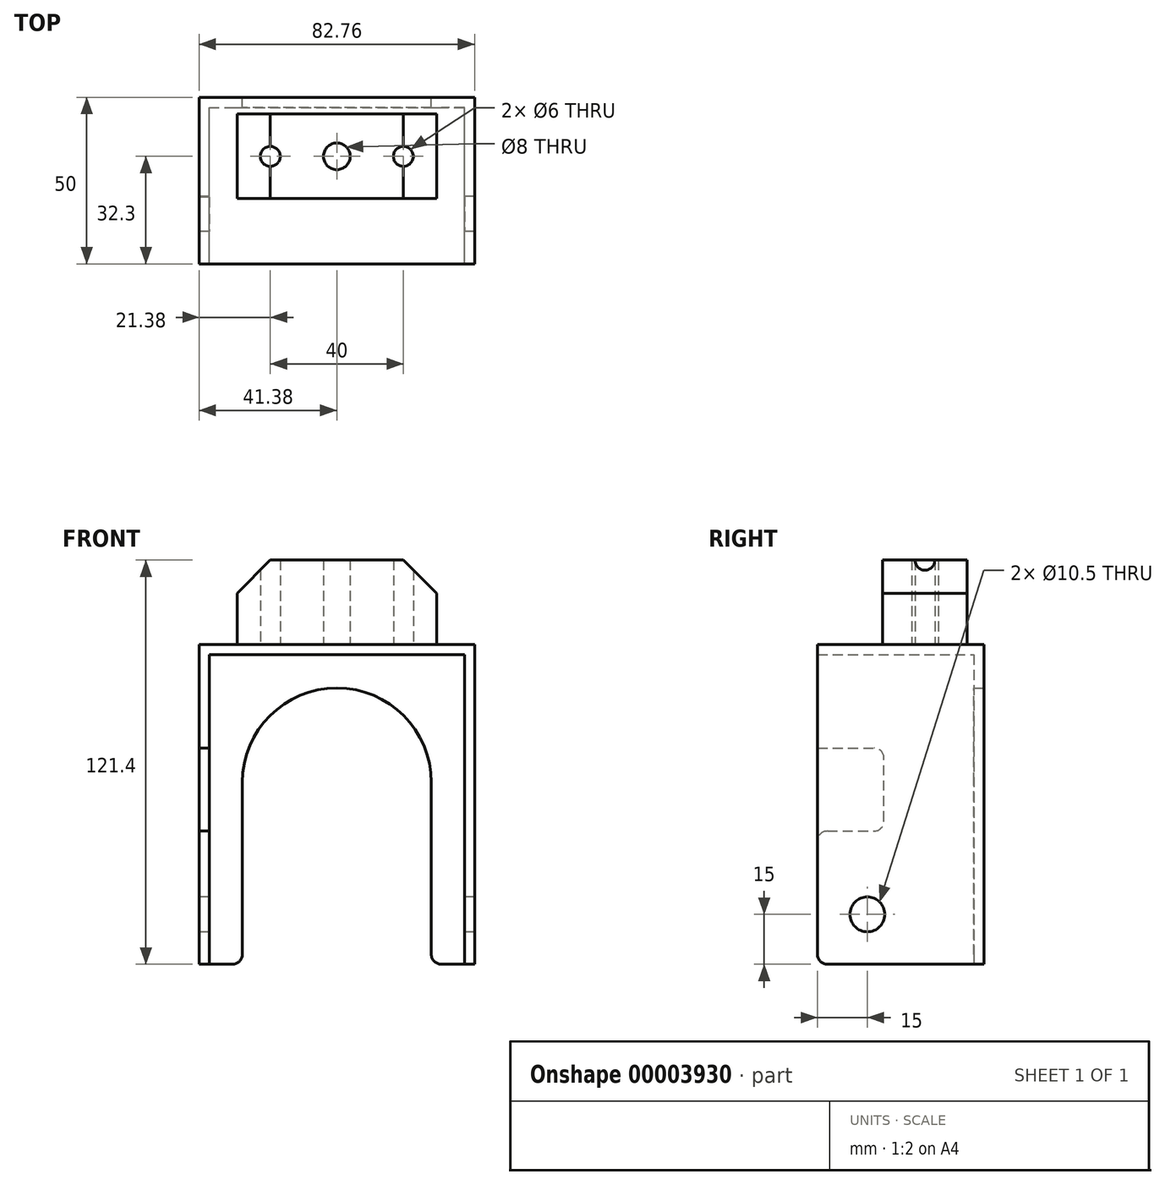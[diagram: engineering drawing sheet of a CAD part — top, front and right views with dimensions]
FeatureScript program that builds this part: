
annotation { "Feature Type Name" : "Feature", "Feature Type Description" : "" }
export const myFeature = defineFeature(function(context is Context, id is Id, definition is map)
    precondition{}
    {
        {
            var Q0;
            Q0=qCreatedBy(makeId("Front.planeOp"),FACE);
            var sketch = newSketch(context, id + "F0", { "sketchPlane" : qUnion([Q0])});
            skLineSegment(sketch, "E0", {"start": v(-38.38, 0) * mm, "end": v(0, 0) * mm});
            skLineSegment(sketch, "E1", {"start": v(0, 0) * mm, "end": v(38.38, 0) * mm});
            skLineSegment(sketch, "E2", {"start": v(-38.38, 0) * mm, "end": v(-38.38, -93) * mm});
            skLineSegment(sketch, "E3", {"start": v(38.38, 0) * mm, "end": v(38.38, -93) * mm});
            skLineSegment(sketch, "E4", {"start": v(-38.38, -93) * mm, "end": v(-28.37, -93) * mm});
            skLineSegment(sketch, "E5", {"start": v(-28.38, -93) * mm, "end": v(-28.38, -38.38) * mm});
            skLineSegment(sketch, "E6", {"start": v(38.38, -93) * mm, "end": v(28.37, -93) * mm});
            skLineSegment(sketch, "E7", {"start": v(28.37, -93) * mm, "end": v(28.37, -38.38) * mm});
            skArc(sketch, "E8", {"start": v(28.38, -38.38) * mm, "mid": v(0, -10) * mm, "end": v(-28.37, -38.38) * mm});
            skLineSegment(sketch, "E9.0", {"start": v(-41.38, 3) * mm, "end": v(-41.38, -93) * mm});
            skLineSegment(sketch, "E9.1", {"start": v(-41.38, 3) * mm, "end": v(0, 3) * mm});
            skLineSegment(sketch, "E9.2", {"start": v(0, 3) * mm, "end": v(41.38, 3) * mm});
            skLineSegment(sketch, "E9.3", {"start": v(41.38, 3) * mm, "end": v(41.38, -93) * mm});
            skLineSegment(sketch, "E10", {"start": v(-41.38, -93) * mm, "end": v(-38.38, -93) * mm});
            skLineSegment(sketch, "E11", {"start": v(38.38, -93) * mm, "end": v(41.38, -93) * mm});
            skLineSegment(sketch, "E12", {"start": v(-16.37, -93) * mm, "end": v(-16.38, -22) * mm, "construction": true});
            skLineSegment(sketch, "E13", {"start": v(-16.38, -22) * mm, "end": v(16.37, -22) * mm, "construction": true});
            skLineSegment(sketch, "E14", {"start": v(16.37, -22) * mm, "end": v(16.38, -93) * mm, "construction": true});
            skLineSegment(sketch, "E15", {"start": v(-41.38, 3) * mm, "end": v(-16.38, -22) * mm, "construction": true});
            skLineSegment(sketch, "E16", {"start": v(16.37, -22) * mm, "end": v(41.38, 3) * mm, "construction": true});
            skSolve(sketch);
        }
        {
            var Q0;
            Q0=makeQuery(id+"F0.imprint","IMPRINT",FACE,{"disambiguationData":[TD([[makeQuery(id+"F0.imprint","IMPRINT",EDGE,{"derivedFrom":sQuery(id+"F0.wireOp",EDGE,"E0")}),-1.0]])]});
            extrude(context, id + "F1", {"entities" : qUnion([Q0]), "depth" : 3 * mm});
        }
        {
            var Q0;
            Q0=makeQuery(id+"F0.imprint","IMPRINT",FACE,{"disambiguationData":[TD([[makeQuery(id+"F0.imprint","IMPRINT",EDGE,{"derivedFrom":sQuery(id+"F0.wireOp",EDGE,"E0")}),1.0]])]});
            extrude(context, id + "F2", {"entities" : qUnion([Q0]), "operationType" : NewBodyOperationType.ADD, "depth" : 50 * mm});
        }
        {
            var Q0;
            Q0=makeQuery(id+"F2.opExtrude","SWEPT_FACE",FACE,{"disambiguationData":[OSD([sQuery(id+"F0.wireOp",EDGE,"E9.0")])]});
            var sketch = newSketch(context, id + "F3", { "sketchPlane" : qUnion([Q0])});
            skCircle(sketch, "E17", {"center": v(35, -78) * mm, "radius": 5.25 * mm});
            skLineSegment(sketch, "E18.bottom", {"start": v(50, -53) * mm, "end": v(30, -53) * mm});
            skLineSegment(sketch, "E18.top", {"start": v(50, -28) * mm, "end": v(30, -28) * mm});
            skLineSegment(sketch, "E18.left", {"start": v(50, -53) * mm, "end": v(50, -28) * mm});
            skLineSegment(sketch, "E18.right", {"start": v(30, -53) * mm, "end": v(30, -28) * mm});
            skSolve(sketch);
        }
        {
            var Q0;
            Q0=makeQuery(id+"F3.imprint","IMPRINT",FACE,{"disambiguationData":[TD([[makeQuery(id+"F3.imprint","IMPRINT",EDGE,{"derivedFrom":sQuery(id+"F3.wireOp",EDGE,"E17")}),1.0]])]});
            extrude(context, id + "F4", {"entities" : qUnion([Q0]), "operationType" : NewBodyOperationType.REMOVE, "endBound" : BoundingType.THROUGH_ALL, "oppositeDirection" : true, "depth" : 25 * mm});
        }
        {
            var Q0;
            Q0=makeQuery(id+"F3.imprint","IMPRINT",FACE,{"disambiguationData":[TD([[makeQuery(id+"F3.imprint","IMPRINT",EDGE,{"derivedFrom":sQuery(id+"F3.wireOp",EDGE,"E18.bottom")}),-1.0]])]});
            extrude(context, id + "F5", {"entities" : qUnion([Q0]), "operationType" : NewBodyOperationType.REMOVE, "endBound" : BoundingType.UP_TO_NEXT, "oppositeDirection" : true, "depth" : 25 * mm});
        }
        {
            var Q0;
            Q0=makeQuery(id+"F5.boolean.opBoolean","COPY",EDGE,{"derivedFrom":makeQuery(id+"F5.opExtrude","SWEPT_EDGE",EDGE,{"disambiguationData":[OSD([sQuery(id+"F3.wireOp",EDGE,"E18.top"),sQuery(id+"F3.wireOp",EDGE,"E18.right")])]})});
            var Q1;
            Q1=makeQuery(id+"F5.boolean.opBoolean","COPY",EDGE,{"derivedFrom":makeQuery(id+"F5.opExtrude","SWEPT_EDGE",EDGE,{"disambiguationData":[OSD([sQuery(id+"F3.wireOp",EDGE,"E18.bottom"),sQuery(id+"F3.wireOp",EDGE,"E18.right")])]})});
            var Q2;
            Q2=makeQuery(id+"F5.boolean.opBoolean","COPY",EDGE,{"derivedFrom":makeQuery(id+"F5.opExtrude","SWEPT_EDGE",EDGE,{"disambiguationData":[OSD([sQuery(id+"F0.wireOp",EDGE,"E9.0"),sQuery(id+"F3.wireOp",EDGE,"E18.top"),sQuery(id+"F3.wireOp",EDGE,"E18.left")])]})});
            var Q3;
            Q3=makeQuery(id+"F5.boolean.opBoolean","COPY",EDGE,{"derivedFrom":makeQuery(id+"F5.opExtrude","SWEPT_EDGE",EDGE,{"disambiguationData":[OSD([sQuery(id+"F0.wireOp",EDGE,"E9.0"),sQuery(id+"F3.wireOp",EDGE,"E18.bottom"),sQuery(id+"F3.wireOp",EDGE,"E18.left")])]})});
            var Q4;
            Q4=makeQuery(id+"F1.opExtrude","SWEPT_EDGE",EDGE,{"disambiguationData":[OSD([sQuery(id+"F0.wireOp",EDGE,"E4"),sQuery(id+"F0.wireOp",EDGE,"E5")])]});
            var Q5;
            Q5=makeQuery(id+"F1.opExtrude","SWEPT_EDGE",EDGE,{"disambiguationData":[OSD([sQuery(id+"F0.wireOp",EDGE,"E6"),sQuery(id+"F0.wireOp",EDGE,"E7")])]});
            var Q6;
            Q6=makeQuery(id+"F2.opExtrude","CAP_EDGE",EDGE,{"disambiguationData":[OSD([sQuery(id+"F0.wireOp",EDGE,"E10")])],"isStart":false});
            var Q7;
            Q7=makeQuery(id+"F2.opExtrude","CAP_EDGE",EDGE,{"disambiguationData":[OSD([sQuery(id+"F0.wireOp",EDGE,"E11")])],"isStart":false});
            fillet(context, id + "F6", {"entities" : qUnion([Q0, Q1, Q2, Q3, Q4, Q5, Q6, Q7]), "radius" : 3 * mm, "tangentPropagation" : true, "allowEdgeOverflow" : false});
        }
        {
            var Q0;
            Q0=makeQuery(id+"F2.opExtrude","SWEPT_FACE",FACE,{"disambiguationData":[OSD([sQuery(id+"F0.wireOp",EDGE,"E9.2")])]});
            var sketch = newSketch(context, id + "F7", { "sketchPlane" : qUnion([Q0])});
            skLineSegment(sketch, "E19.top", {"start": v(-30, -30.4) * mm, "end": v(30, -30.4) * mm});
            skLineSegment(sketch, "E19.left", {"start": v(-30, -5) * mm, "end": v(-30, -30.4) * mm});
            skLineSegment(sketch, "E19.right", {"start": v(30, -5) * mm, "end": v(30, -30.4) * mm});
            skLineSegment(sketch, "E20", {"start": v(-30, -5) * mm, "end": v(0, -5) * mm});
            skLineSegment(sketch, "E21", {"start": v(0, -5) * mm, "end": v(30, -5) * mm});
            skPoint(sketch, "E22", {"position": v(-30, -17.7) * mm});
            skPoint(sketch, "E23", {"position": v(30, -17.7) * mm});
            skCircle(sketch, "E24", {"center": v(-20, -17.7) * mm, "radius": 3 * mm});
            skCircle(sketch, "E25", {"center": v(20, -17.7) * mm, "radius": 3 * mm});
            skCircle(sketch, "E26", {"center": v(0, -17.7) * mm, "radius": 4 * mm});
            skSolve(sketch);
        }
        {
            var Q0;
            Q0=makeQuery(id+"F7.imprint","IMPRINT",FACE,{"disambiguationData":[TD([[makeQuery(id+"F7.imprint","IMPRINT",EDGE,{"derivedFrom":sQuery(id+"F7.wireOp",EDGE,"E19.top")}),1.0]])]});
            extrude(context, id + "F8", {"entities" : qUnion([Q0]), "depth" : 25.4 * mm});
        }
        {
            var Q0;
            Q0=makeQuery(id+"F8.opExtrude","CAP_EDGE",EDGE,{"disambiguationData":[OSD([sQuery(id+"F7.wireOp",EDGE,"E19.right")])],"isStart":false});
            var Q1;
            Q1=makeQuery(id+"F8.opExtrude","CAP_EDGE",EDGE,{"disambiguationData":[OSD([sQuery(id+"F7.wireOp",EDGE,"E19.left")])],"isStart":false});
            chamfer(context, id + "F9", {"entities" : qUnion([Q0, Q1]), "width" : 10 * mm, "tangentPropagation" : true});
        }
    });
